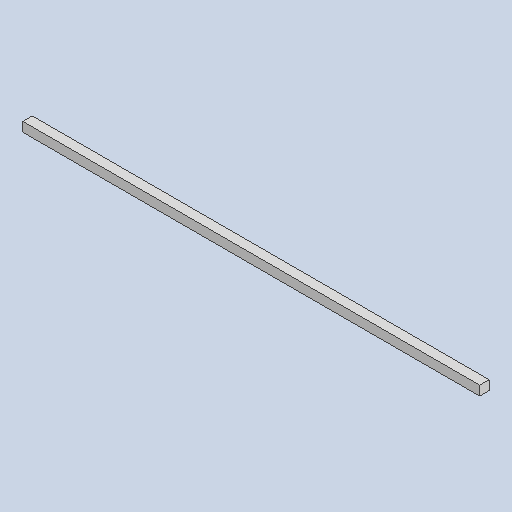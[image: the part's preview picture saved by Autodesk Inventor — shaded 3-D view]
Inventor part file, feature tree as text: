
AUTODESK INVENTOR PART (.ipt)
format: ipt  version: 2023 (Build 270158000, 158)  size: 82,944 bytes
history: native  units: mm
features: extrude x1, sketch x1
ambient origin geometry x8: Origin, YZ Plane, XZ Plane, XY Plane, X Axis, Y Axis, Z Axis, Center Point
bodies: Solid1 (feature_tree)
feature tree (2):
  extrude  "Extrusion1"  Depth=30.0mm TaperAngle=0.0deg
  sketch  "Sketch1"  dims[d0=30.0mm d1=30.0mm d2=0.0mm d3=1450.0mm]
